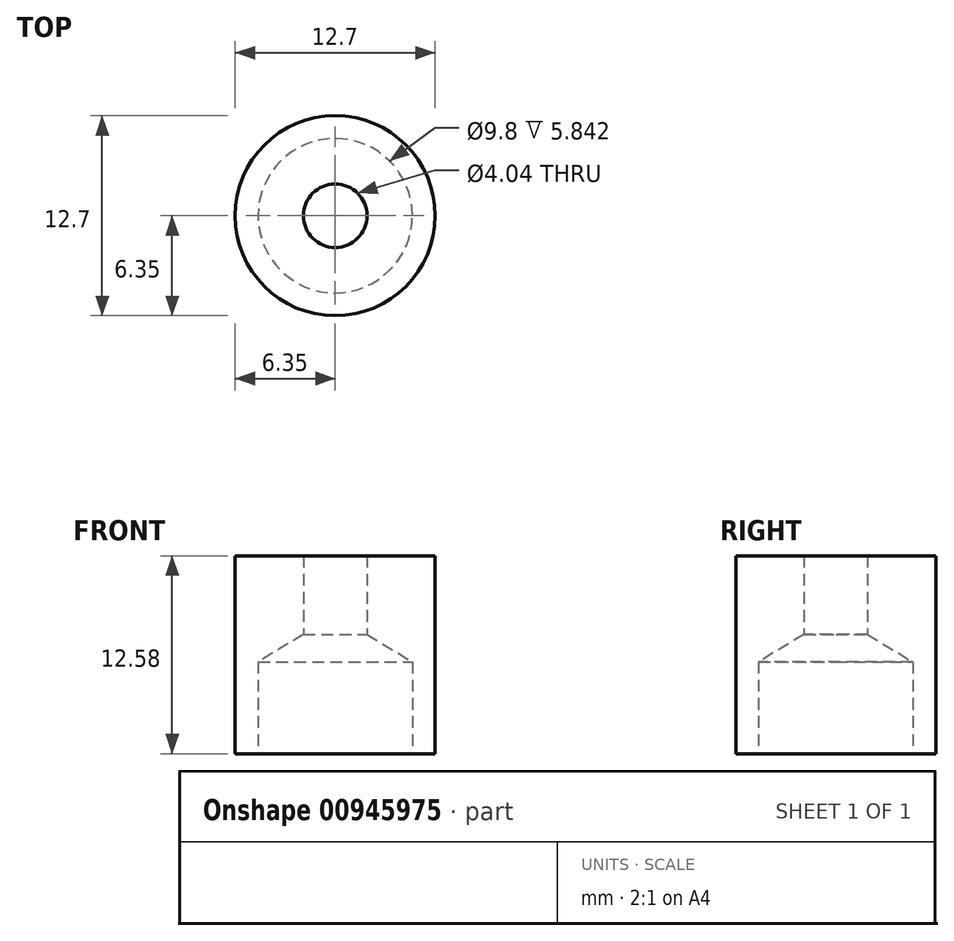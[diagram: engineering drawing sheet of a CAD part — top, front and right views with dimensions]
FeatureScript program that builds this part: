
annotation { "Feature Type Name" : "Feature", "Feature Type Description" : "" }
export const myFeature = defineFeature(function(context is Context, id is Id, definition is map)
    precondition{}
    {
        {
            var Q0;
            Q0=qCreatedBy(makeId("Top.planeOp"),FACE);
            cPlane(context, id + "F0", {"entities" : qUnion([Q0]), "cplaneType" : CPlaneType.OFFSET, "offset" : 4.44 * mm, "oppositeDirection" : true, "width" : 152.4 * mm, "height" : 152.4 * mm});
        }
        {
            var Q0;
            Q0=qCreatedBy(makeId("Top.planeOp"),FACE);
            cPlane(context, id + "F1", {"entities" : qUnion([Q0]), "cplaneType" : CPlaneType.OFFSET, "offset" : 8.13 * mm, "width" : 152.4 * mm, "height" : 152.4 * mm});
        }
        {
            var Q0;
            Q0=qCreatedBy(makeId("Top.planeOp"),FACE);
            var sketch = newSketch(context, id + "F2", { "sketchPlane" : qUnion([Q0])});
            skCircle(sketch, "E0", {"center": v(0, 0) * mm, "radius": 6.35 * mm});
            skSolve(sketch);
        }
        {
            var Q0;
            Q0=qSketchRegion(id+"F2",true);
            var Q1;
            Q1=qCreatedBy(id+"F0.planeOp",FACE);
            extrude(context, id + "F3", {"entities" : qUnion([Q0]), "endBound" : BoundingType.UP_TO_SURFACE, "oppositeDirection" : true, "depth" : 25.4 * mm, "endBoundEntityFace" : qUnion([Q1]), "offsetDistance" : 25.4 * mm});
        }
        {
            var Q0;
            Q0=qCreatedBy(makeId("Top.planeOp"),FACE);
            var sketch = newSketch(context, id + "F4", { "sketchPlane" : qUnion([Q0])});
            skCircle(sketch, "E1", {"center": v(0, 0) * mm, "radius": 9.53 * mm});
            skSolve(sketch);
        }
        {
            var Q0;
            Q0=makeQuery(id+"F4.imprint","IMPRINT",FACE,{"disambiguationData":[TD([[makeQuery(id+"F4.imprint","IMPRINT",EDGE,{"derivedFrom":sQuery(id+"F4.wireOp",EDGE,"E1")}),1.0]])]});
            var Q1;
            Q1=qCreatedBy(id+"F1.planeOp",FACE);
            extrude(context, id + "F5", {"entities" : qUnion([Q0]), "operationType" : NewBodyOperationType.ADD, "endBound" : BoundingType.UP_TO_SURFACE, "depth" : 25.4 * mm, "endBoundEntityFace" : qUnion([Q1]), "offsetDistance" : 25.4 * mm});
        }
        {
            var Q0;
            Q0=qCreatedBy(makeId("Top.planeOp"),FACE);
            var sketch = newSketch(context, id + "F6", { "sketchPlane" : qUnion([Q0])});
            skLineSegment(sketch, "E2.bottom", {"start": v(19.05, -7.47) * mm, "end": v(-19.05, -7.47) * mm});
            skLineSegment(sketch, "E2.top", {"start": v(19.05, 7.47) * mm, "end": v(-19.05, 7.47) * mm});
            skLineSegment(sketch, "E2.left", {"start": v(19.05, -7.47) * mm, "end": v(19.05, 7.47) * mm, "construction": true});
            skLineSegment(sketch, "E2.right", {"start": v(-19.05, -7.47) * mm, "end": v(-19.05, 7.47) * mm, "construction": true});
            skPoint(sketch, "E2.middle", {"position": v(0, 0) * mm});
            skLineSegment(sketch, "E3.bottom", {"start": v(-19.05, 7.47) * mm, "end": v(19.05, 7.47) * mm});
            skLineSegment(sketch, "E3.top", {"start": v(-19.05, 22.4) * mm, "end": v(19.05, 22.4) * mm});
            skLineSegment(sketch, "E3.left", {"start": v(-19.05, 7.47) * mm, "end": v(-19.05, 22.4) * mm});
            skLineSegment(sketch, "E3.right", {"start": v(19.05, 7.47) * mm, "end": v(19.05, 22.4) * mm});
            skLineSegment(sketch, "E4.bottom", {"start": v(-19.05, -7.47) * mm, "end": v(19.05, -7.47) * mm});
            skLineSegment(sketch, "E4.top", {"start": v(-19.05, -22.4) * mm, "end": v(19.05, -22.4) * mm});
            skLineSegment(sketch, "E4.left", {"start": v(-19.05, -7.47) * mm, "end": v(-19.05, -22.4) * mm});
            skLineSegment(sketch, "E4.right", {"start": v(19.05, -7.47) * mm, "end": v(19.05, -22.4) * mm});
            skSolve(sketch);
        }
        {
            var Q0;
            Q0=qCreatedBy(id+"F0.planeOp",FACE);
            var sketch = newSketch(context, id + "F7", { "sketchPlane" : qUnion([Q0])});
            skPoint(sketch, "E5", {"position": v(0, 0) * mm});
            skSolve(sketch);
        }
        {
            var Q0;
            Q0=qSketchRegion(id+"F6",true);
            extrude(context, id + "F8", {"entities" : qUnion([Q0]), "operationType" : NewBodyOperationType.REMOVE, "depth" : 25.4 * mm, "offsetDistance" : 25.4 * mm});
        }
        {
            var Q0;
            Q0=sQuery(id+"F7.wireOp",VERTEX,"E5");
            var Q1;
            Q1=makeQuery(id+"F3.opExtrude","SWEPT_BODY",BODY,{"disambiguationData":[OSD([sQuery(id+"F2.wireOp",EDGE,"E0")])]});
            hole(context, id + "F9", {"style" : HoleStyle.SIMPLE, "endStyle" : HoleEndStyle.BLIND, "oppositeDirection" : true, "standardTappedOrClearance" : lookupTablePath({ "standard" : "ANSI", "size" : "W (0.39)", "type" : "Drilled" }), "standardBlindInLast" : lookupTablePath({ "standard" : "ANSI", "size" : "W (0.39)", "type" : "Drilled" }), "holeDiameter" : 9.8 * mm, "majorDiameter" : 6.35 * mm, "holeDepth" : 5.84 * mm, "tappedDepth" : 12.7 * mm, "tapClearance" : 3, "locations" : qUnion([Q0]), "scope" : qUnion([Q1])});
        }
        {
            var Q0;
            Q0=sQuery(id+"F7.wireOp",VERTEX,"E5");
            var Q1;
            Q1=makeQuery(id+"F3.opExtrude","SWEPT_BODY",BODY,{"disambiguationData":[OSD([sQuery(id+"F2.wireOp",EDGE,"E0")])]});
            hole(context, id + "F10", {"style" : HoleStyle.SIMPLE, "endStyle" : HoleEndStyle.THROUGH, "oppositeDirection" : true, "standardTappedOrClearance" : lookupTablePath({ "standard" : "ANSI", "size" : "#21 (0.16)", "type" : "Drilled" }), "standardBlindInLast" : lookupTablePath({ "standard" : "ANSI", "size" : "#21 (0.16)", "type" : "Drilled" }), "holeDiameter" : 4.04 * mm, "majorDiameter" : 6.35 * mm, "tappedDepth" : 12.7 * mm, "tapClearance" : 3, "locations" : qUnion([Q0]), "scope" : qUnion([Q1])});
        }
        {
            var Q0;
            Q0=qCreatedBy(id+"F0.planeOp",FACE);
            var sketch = newSketch(context, id + "F11", { "sketchPlane" : qUnion([Q0])});
            skCircle(sketch, "E6", {"center": v(0, 0) * mm, "radius": 6.35 * mm});
            skCircle(sketch, "E7", {"center": v(0, 0) * mm, "radius": 22.56 * mm});
            skSolve(sketch);
        }
        {
            var Q0;
            Q0=makeQuery(id+"F11.imprint","IMPRINT",FACE,{"disambiguationData":[TD([[makeQuery(id+"F11.imprint","IMPRINT",EDGE,{"derivedFrom":sQuery(id+"F11.wireOp",EDGE,"E6")}),-1.0]])]});
            extrude(context, id + "F12", {"entities" : qUnion([Q0]), "operationType" : NewBodyOperationType.REMOVE, "depth" : 25.4 * mm, "offsetDistance" : 25.4 * mm});
        }
    });
